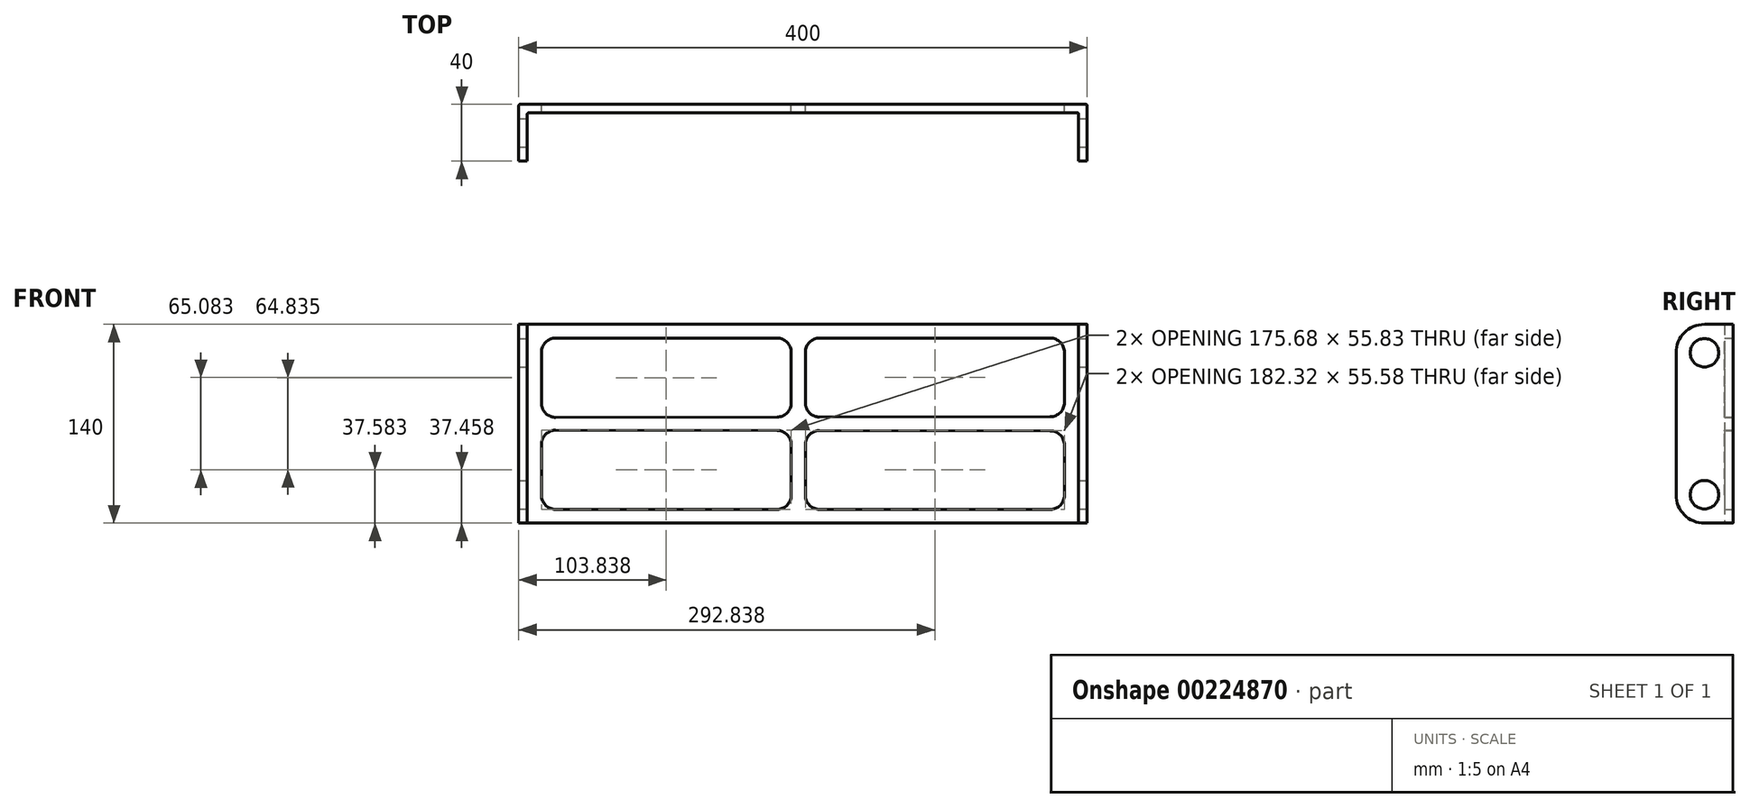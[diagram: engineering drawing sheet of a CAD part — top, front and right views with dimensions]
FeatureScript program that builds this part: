
annotation { "Feature Type Name" : "Feature", "Feature Type Description" : "" }
export const myFeature = defineFeature(function(context is Context, id is Id, definition is map)
    precondition{}
    {
        {
            var Q0;
            Q0=qCreatedBy(makeId("Top.planeOp"),FACE);
            var sketch = newSketch(context, id + "F0", { "sketchPlane" : qUnion([Q0])});
            skLineSegment(sketch, "E0", {"start": v(-195.68, 14.57) * mm, "end": v(202.32, 14.57) * mm});
            skLineSegment(sketch, "E1", {"start": v(203.32, 13.57) * mm, "end": v(203.32, -25.43) * mm});
            skLineSegment(sketch, "E2.0", {"start": v(-189.68, 8.57) * mm, "end": v(196.32, 8.57) * mm});
            skLineSegment(sketch, "E3.0", {"start": v(197.32, 7.57) * mm, "end": v(197.32, -25.43) * mm});
            skLineSegment(sketch, "E4", {"start": v(-196.68, 13.57) * mm, "end": v(-196.68, -25.43) * mm});
            skLineSegment(sketch, "E5.0", {"start": v(-190.68, 7.57) * mm, "end": v(-190.68, -25.43) * mm});
            skLineSegment(sketch, "E6", {"start": v(-196.68, -25.43) * mm, "end": v(-190.68, -25.43) * mm});
            skLineSegment(sketch, "E7", {"start": v(197.32, -25.43) * mm, "end": v(203.32, -25.43) * mm});
            skPoint(sketch, "E8.visualSharp", {"position": v(-196.68, 14.57) * mm});
            skArc(sketch, "E8.filletArc", {"start": v(-195.68, 14.57) * mm, "mid": v(-196.4, 14.28) * mm, "end": v(-196.68, 13.57) * mm});
            skPoint(sketch, "E9.visualSharp", {"position": v(-190.68, 8.57) * mm});
            skArc(sketch, "E9.filletArc", {"start": v(-189.68, 8.57) * mm, "mid": v(-190.4, 8.28) * mm, "end": v(-190.68, 7.57) * mm});
            skPoint(sketch, "E10.visualSharp", {"position": v(203.32, 14.57) * mm});
            skArc(sketch, "E10.filletArc", {"start": v(203.32, 13.57) * mm, "mid": v(203.02, 14.28) * mm, "end": v(202.32, 14.57) * mm});
            skPoint(sketch, "E11.visualSharp", {"position": v(197.32, 8.57) * mm});
            skArc(sketch, "E11.filletArc", {"start": v(197.32, 7.57) * mm, "mid": v(197.02, 8.28) * mm, "end": v(196.32, 8.57) * mm});
            skSolve(sketch);
        }
        {
            var Q0;
            Q0=qSketchRegion(id+"F0",true);
            extrude(context, id + "F1", {"entities" : qUnion([Q0]), "depth" : 140 * mm});
        }
        {
            var Q0;
            Q0=makeQuery(id+"F1.opExtrude","SWEPT_FACE",FACE,{"disambiguationData":[OSD([sQuery(id+"F0.wireOp",EDGE,"E1")])]});
            var sketch = newSketch(context, id + "F2", { "sketchPlane" : qUnion([Q0])});
            skLineSegment(sketch, "E12", {"start": v(-66.18, 140.53) * mm, "end": v(-66.18, -19.47) * mm});
            skLineSegment(sketch, "E13", {"start": v(-66.18, -19.47) * mm, "end": v(3.82, -19.47) * mm});
            skLineSegment(sketch, "E14", {"start": v(3.82, -19.47) * mm, "end": v(3.82, 0) * mm});
            skLineSegment(sketch, "E15", {"start": v(3.82, 0) * mm, "end": v(-5.43, 0) * mm});
            skLineSegment(sketch, "E16", {"start": v(-25.43, 20) * mm, "end": v(-25.43, 120) * mm});
            skLineSegment(sketch, "E17", {"start": v(-5.43, 140) * mm, "end": v(3.82, 140) * mm});
            skLineSegment(sketch, "E18", {"start": v(3.82, 140) * mm, "end": v(3.82, 140.53) * mm});
            skLineSegment(sketch, "E19", {"start": v(3.82, 140.53) * mm, "end": v(-66.18, 140.53) * mm});
            skPoint(sketch, "E20.visualSharp", {"position": v(-25.43, 140) * mm});
            skArc(sketch, "E20.filletArc", {"start": v(-5.43, 140) * mm, "mid": v(-19.57, 134.14) * mm, "end": v(-25.43, 120) * mm});
            skPoint(sketch, "E21.visualSharp", {"position": v(-25.43, 0) * mm});
            skArc(sketch, "E21.filletArc", {"start": v(-25.43, 20) * mm, "mid": v(-19.57, 5.86) * mm, "end": v(-5.43, 0) * mm});
            skLineSegment(sketch, "E22", {"start": v(-25.43, 20) * mm, "end": v(48.37, 20) * mm, "construction": true});
            skCircle(sketch, "E23", {"center": v(-5.43, 20) * mm, "radius": 10 * mm});
            skLineSegment(sketch, "E24", {"start": v(13.57, 70) * mm, "end": v(-40.82, 70) * mm, "construction": true});
            skCircle(sketch, "E25.MirrorC", {"center": v(-5.43, 120) * mm, "radius": 10 * mm});
            skSolve(sketch);
        }
        {
            var Q0;
            Q0=qSketchRegion(id+"F2",true);
            extrude(context, id + "F3", {"entities" : qUnion([Q0]), "operationType" : NewBodyOperationType.REMOVE, "endBound" : BoundingType.THROUGH_ALL, "oppositeDirection" : true, "depth" : 25 * mm});
        }
        {
            var Q0;
            Q0=makeQuery(id+"F1.opExtrude","SWEPT_FACE",FACE,{"disambiguationData":[OSD([sQuery(id+"F0.wireOp",EDGE,"E0")])]});
            var sketch = newSketch(context, id + "F4", { "sketchPlane" : qUnion([Q0])});
            skLineSegment(sketch, "E26.0", {"start": v(-177.33, 74.97) * mm, "end": v(-15.01, 74.75) * mm});
            skLineSegment(sketch, "E27.0", {"start": v(-187.32, 120.33) * mm, "end": v(-187.32, 84.97) * mm});
            skLineSegment(sketch, "E28", {"start": v(180.68, 120.33) * mm, "end": v(180.68, 84.5) * mm});
            skLineSegment(sketch, "E29", {"start": v(-177.32, 130.33) * mm, "end": v(-15, 130.33) * mm});
            skPoint(sketch, "E30.orphan", {"position": v(-187.32, 140) * mm});
            skPoint(sketch, "E31.orphan", {"position": v(180.68, 140) * mm});
            skPoint(sketch, "E32.orphan", {"position": v(180.68, 0) * mm});
            skPoint(sketch, "E33.visualSharp", {"position": v(-187.32, 130.33) * mm});
            skArc(sketch, "E33.filletArc", {"start": v(-177.32, 130.33) * mm, "mid": v(-184.39, 127.4) * mm, "end": v(-187.32, 120.33) * mm});
            skPoint(sketch, "E34.visualSharp", {"position": v(180.68, 130.33) * mm});
            skArc(sketch, "E34.filletArc", {"start": v(180.68, 120.33) * mm, "mid": v(177.76, 127.4) * mm, "end": v(170.68, 130.33) * mm});
            skPoint(sketch, "E35.visualSharp", {"position": v(-187.32, 74.98) * mm});
            skArc(sketch, "E35.filletArc", {"start": v(-187.32, 84.97) * mm, "mid": v(-184.4, 77.9) * mm, "end": v(-177.33, 74.97) * mm});
            skPoint(sketch, "E36.visualSharp", {"position": v(180.68, 74.49) * mm});
            skArc(sketch, "E36.filletArc", {"start": v(170.67, 74.5) * mm, "mid": v(177.75, 77.43) * mm, "end": v(180.68, 84.5) * mm});
            skLineSegment(sketch, "E37", {"start": v(-202.32, 70) * mm, "end": v(195.68, 70) * mm, "construction": true});
            skLineSegment(sketch, "E38.0", {"start": v(-5, 84.75) * mm, "end": v(-5, 120.33) * mm});
            skLineSegment(sketch, "E39.0", {"start": v(5, 84.7) * mm, "end": v(5, 120.33) * mm});
            skLineSegment(sketch, "E40.trimOffspring", {"start": v(15, 130.33) * mm, "end": v(170.68, 130.33) * mm});
            skPoint(sketch, "E41.start.orphan", {"position": v(0, 74.73) * mm});
            skLineSegment(sketch, "E42.trimOffspring", {"start": v(14.99, 74.7) * mm, "end": v(170.67, 74.5) * mm});
            skArc(sketch, "E43.filletArc", {"start": v(5, 84.7) * mm, "mid": v(7.92, 77.64) * mm, "end": v(14.99, 74.7) * mm});
            skPoint(sketch, "E44.visualSharp", {"position": v(5, 130.33) * mm});
            skArc(sketch, "E44.filletArc", {"start": v(15, 130.33) * mm, "mid": v(7.93, 127.4) * mm, "end": v(5, 120.33) * mm});
            skPoint(sketch, "E45.visualSharp", {"position": v(-5, 130.33) * mm});
            skArc(sketch, "E45.filletArc", {"start": v(-5, 120.33) * mm, "mid": v(-7.93, 127.4) * mm, "end": v(-15, 130.33) * mm});
            skArc(sketch, "E46.filletArc", {"start": v(-15.01, 74.75) * mm, "mid": v(-7.93, 77.67) * mm, "end": v(-5, 84.75) * mm});
            skArc(sketch, "E47.MirrorCS", {"start": v(-177.32, 9.67) * mm, "mid": v(-184.39, 12.6) * mm, "end": v(-187.32, 19.67) * mm});
            skArc(sketch, "E48.MirrorCS", {"start": v(-5, 19.67) * mm, "mid": v(-7.93, 12.6) * mm, "end": v(-15, 9.67) * mm});
            skArc(sketch, "E49.MirrorCS", {"start": v(15, 9.67) * mm, "mid": v(7.93, 12.6) * mm, "end": v(5, 19.67) * mm});
            skArc(sketch, "E50.MirrorCS", {"start": v(-187.32, 55.03) * mm, "mid": v(-184.4, 62.1) * mm, "end": v(-177.33, 65.03) * mm});
            skArc(sketch, "E51.MirrorCS", {"start": v(180.68, 19.67) * mm, "mid": v(177.76, 12.6) * mm, "end": v(170.68, 9.67) * mm});
            skArc(sketch, "E52.MirrorCS", {"start": v(170.67, 65.5) * mm, "mid": v(177.75, 62.57) * mm, "end": v(180.68, 55.5) * mm});
            skLineSegment(sketch, "E53.MirrorCS", {"start": v(15, 9.67) * mm, "end": v(170.68, 9.67) * mm});
            skLineSegment(sketch, "E54.MirrorCS", {"start": v(5, 55.3) * mm, "end": v(5, 19.67) * mm});
            skPoint(sketch, "E55.MirrorP", {"position": v(-187.32, 9.67) * mm});
            skPoint(sketch, "E56.MirrorP", {"position": v(-187.32, 65.02) * mm});
            skArc(sketch, "E57.MirrorCS", {"start": v(-15.01, 65.25) * mm, "mid": v(-7.93, 62.33) * mm, "end": v(-5, 55.25) * mm});
            skLineSegment(sketch, "E58.MirrorCS", {"start": v(-177.32, 9.67) * mm, "end": v(-15, 9.67) * mm});
            skPoint(sketch, "E59.MirrorP", {"position": v(180.68, 9.67) * mm});
            skPoint(sketch, "E60.MirrorP", {"position": v(5, 9.67) * mm});
            skArc(sketch, "E61.MirrorCS", {"start": v(5, 55.3) * mm, "mid": v(7.92, 62.36) * mm, "end": v(14.99, 65.3) * mm});
            skLineSegment(sketch, "E62.MirrorCS", {"start": v(180.68, 19.67) * mm, "end": v(180.68, 55.5) * mm});
            skLineSegment(sketch, "E63.MirrorCS", {"start": v(-177.33, 65.03) * mm, "end": v(-15.01, 65.25) * mm});
            skLineSegment(sketch, "E64.MirrorCS", {"start": v(14.99, 65.3) * mm, "end": v(170.67, 65.5) * mm});
            skPoint(sketch, "E65.MirrorP", {"position": v(-5, 9.67) * mm});
            skPoint(sketch, "E66.MirrorP", {"position": v(0, 65.27) * mm});
            skPoint(sketch, "E67.MirrorP", {"position": v(180.68, 65.51) * mm});
            skPoint(sketch, "E68.MirrorP", {"position": v(-187.32, 0) * mm});
            skLineSegment(sketch, "E69.MirrorCS", {"start": v(-187.32, 19.67) * mm, "end": v(-187.32, 55.03) * mm});
            skLineSegment(sketch, "E70.MirrorCS", {"start": v(-5, 55.25) * mm, "end": v(-5, 19.67) * mm});
            skSolve(sketch);
        }
        {
            var Q0;
            Q0 = qSketchRegion(id + "F4", true);
            extrude(context, id + "F5", {"entities" : qUnion([Q0]), "operationType" : NewBodyOperationType.REMOVE, "endBound" : BoundingType.THROUGH_ALL, "oppositeDirection" : true, "depth" : 25 * mm});
        }
    });
